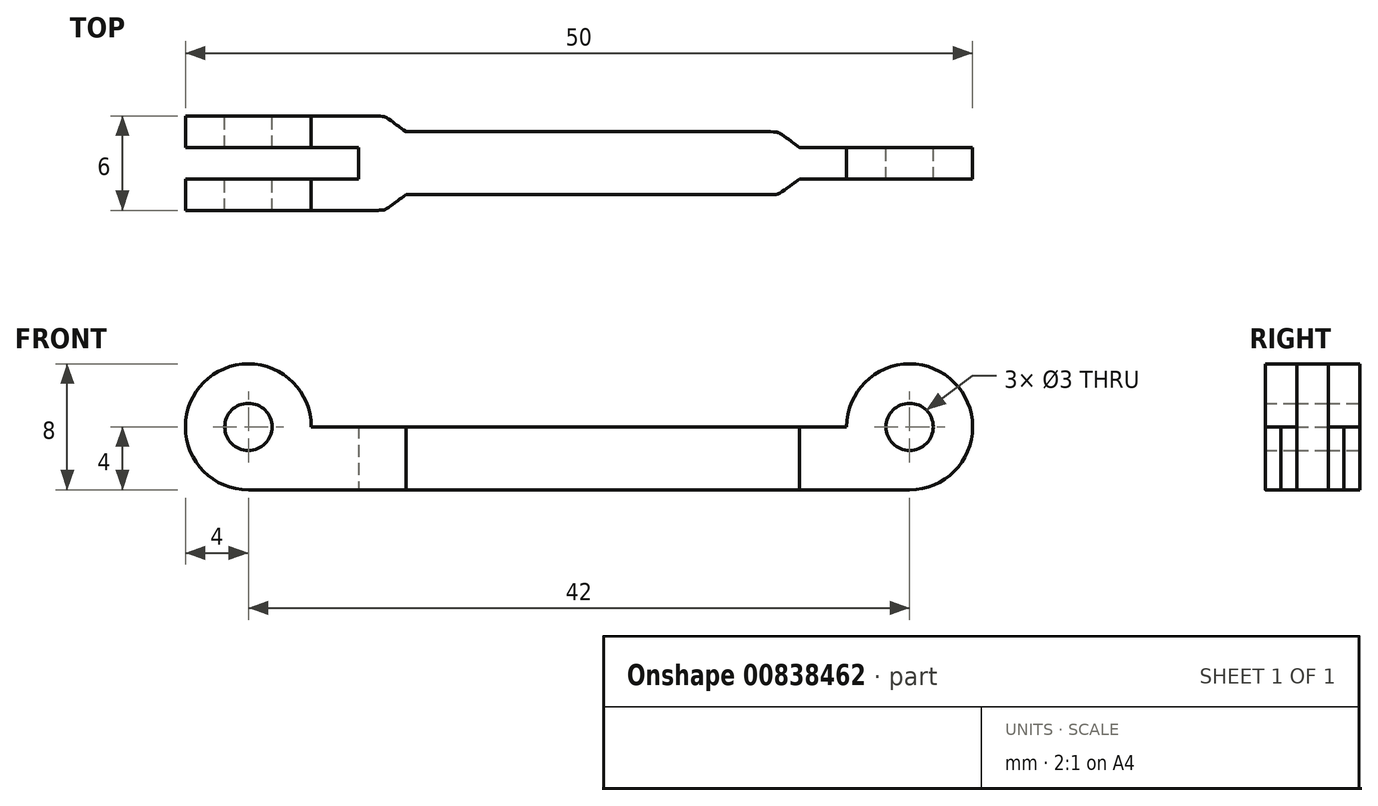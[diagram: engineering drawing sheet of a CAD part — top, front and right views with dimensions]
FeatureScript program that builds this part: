
annotation { "Feature Type Name" : "Feature", "Feature Type Description" : "" }
export const myFeature = defineFeature(function(context is Context, id is Id, definition is map)
    precondition{}
    {
        {
            var Q0;
            Q0=qCreatedBy(makeId("Front.planeOp"),FACE);
            var sketch = newSketch(context, id + "F0", { "sketchPlane" : qUnion([Q0])});
            skLineSegment(sketch, "E0.bottom", {"start": v(21, 2) * mm, "end": v(-21, 2) * mm});
            skLineSegment(sketch, "E0.top", {"start": v(21, -2) * mm, "end": v(-21, -2) * mm});
            skLineSegment(sketch, "E0.left", {"start": v(21, 2) * mm, "end": v(21, -2) * mm});
            skLineSegment(sketch, "E0.right", {"start": v(-21, 2) * mm, "end": v(-21, -2) * mm});
            skPoint(sketch, "E0.middle", {"position": v(0, 0) * mm});
            skLineSegment(sketch, "E1", {"start": v(-14, 2) * mm, "end": v(-14, -2) * mm});
            skLineSegment(sketch, "E2", {"start": v(-11, 2) * mm, "end": v(-11, -2) * mm});
            skCircle(sketch, "E3", {"center": v(21, 2) * mm, "radius": 4 * mm});
            skCircle(sketch, "E4", {"center": v(-21, 2) * mm, "radius": 4 * mm});
            skCircle(sketch, "E5", {"center": v(21, 2) * mm, "radius": 1.5 * mm});
            skCircle(sketch, "E6", {"center": v(-21, 2) * mm, "radius": 1.5 * mm});
            skLineSegment(sketch, "E7", {"start": v(14, 2) * mm, "end": v(14, -2) * mm});
            skSolve(sketch);
        }
        {
            var Q0;
            {var subQ0=sQuery(id+"F0.wireOp",EDGE,"E4");var subQ1=sQuery(id+"F0.wireOp",EDGE,"E0.bottom");var subQ2=makeQuery(id+"F0.imprint","INTERSECT",VERTEX,{"derivedFrom":[subQ1,subQ0]});Q0=makeQuery(id+"F0.imprint","IMPRINT",FACE,{"disambiguationData":[TD([[makeQuery(id+"F0.imprint","IMPRINT",EDGE,{"disambiguationData":[TD([[subQ2,-1.0]])],"derivedFrom":subQ1}),-1.0]])]});}
            var Q1;
            {var subQ0=sQuery(id+"F0.wireOp",EDGE,"E4");var subQ1=sQuery(id+"F0.wireOp",EDGE,"E0.bottom");var subQ2=makeQuery(id+"F0.imprint","INTERSECT",VERTEX,{"derivedFrom":[subQ1,subQ0]});Q1=makeQuery(id+"F0.imprint","IMPRINT",FACE,{"disambiguationData":[TD([[makeQuery(id+"F0.imprint","IMPRINT",EDGE,{"disambiguationData":[TD([[subQ2,-1.0]])],"derivedFrom":subQ1}),1.0]])]});}
            var Q2;
            {var subQ0=sQuery(id+"F0.wireOp",EDGE,"E1");Q2=makeQuery(id+"F0.imprint","IMPRINT",FACE,{"disambiguationData":[TD([[makeQuery(id+"F0.imprint","IMPRINT",EDGE,{"derivedFrom":subQ0}),-1.0]])]});}
            var Q3;
            {var subQ0=sQuery(id+"F0.wireOp",EDGE,"E1");Q3=makeQuery(id+"F0.imprint","IMPRINT",FACE,{"disambiguationData":[TD([[makeQuery(id+"F0.imprint","IMPRINT",EDGE,{"derivedFrom":subQ0}),1.0]])]});}
            extrude(context, id + "F1", {"entities" : qUnion([Q0, Q1, Q2, Q3]), "flatOperationType" : FlatOperationType.REMOVE, "depth" : 6 * mm, "offsetDistance" : 25 * mm, "domain" : OperationDomain.MODEL, "symmetric" : true});
        }
        {
            var Q0;
            {var subQ0=sQuery(id+"F0.wireOp",EDGE,"E2");Q0=makeQuery(id+"F0.imprint","IMPRINT",FACE,{"disambiguationData":[TD([[makeQuery(id+"F0.imprint","IMPRINT",EDGE,{"derivedFrom":subQ0}),1.0]])]});}
            extrude(context, id + "F2", {"entities" : qUnion([Q0]), "operationType" : NewBodyOperationType.ADD, "depth" : 4 * mm, "offsetDistance" : 25 * mm, "symmetric" : true});
        }
        {
            var Q0;
            {var subQ0=sQuery(id+"F0.wireOp",EDGE,"E7");Q0=makeQuery(id+"F0.imprint","IMPRINT",FACE,{"disambiguationData":[TD([[makeQuery(id+"F0.imprint","IMPRINT",EDGE,{"derivedFrom":subQ0}),1.0]])]});}
            var Q1;
            {var subQ0=sQuery(id+"F0.wireOp",EDGE,"E3");var subQ1=sQuery(id+"F0.wireOp",EDGE,"E0.bottom");var subQ2=makeQuery(id+"F0.imprint","INTERSECT",VERTEX,{"derivedFrom":[subQ1,subQ0]});Q1=makeQuery(id+"F0.imprint","IMPRINT",FACE,{"disambiguationData":[TD([[makeQuery(id+"F0.imprint","IMPRINT",EDGE,{"disambiguationData":[TD([[subQ2,1.0]])],"derivedFrom":subQ1}),1.0]])]});}
            var Q2;
            {var subQ0=sQuery(id+"F0.wireOp",EDGE,"E3");var subQ1=sQuery(id+"F0.wireOp",EDGE,"E0.bottom");var subQ2=makeQuery(id+"F0.imprint","INTERSECT",VERTEX,{"derivedFrom":[subQ1,subQ0]});Q2=makeQuery(id+"F0.imprint","IMPRINT",FACE,{"disambiguationData":[TD([[makeQuery(id+"F0.imprint","IMPRINT",EDGE,{"disambiguationData":[TD([[subQ2,1.0]])],"derivedFrom":subQ1}),-1.0]])]});}
            extrude(context, id + "F3", {"entities" : qUnion([Q0, Q1, Q2]), "operationType" : NewBodyOperationType.ADD, "depth" : 2 * mm, "offsetDistance" : 25 * mm, "symmetric" : true});
        }
        {
            var Q0;
            {var subQ0=sQuery(id+"F0.wireOp",EDGE,"E1");Q0=makeQuery(id+"F0.imprint","IMPRINT",FACE,{"disambiguationData":[TD([[makeQuery(id+"F0.imprint","IMPRINT",EDGE,{"derivedFrom":subQ0}),-1.0]])]});}
            var Q1;
            {var subQ0=sQuery(id+"F0.wireOp",EDGE,"E4");var subQ1=sQuery(id+"F0.wireOp",EDGE,"E0.bottom");var subQ2=makeQuery(id+"F0.imprint","INTERSECT",VERTEX,{"derivedFrom":[subQ1,subQ0]});Q1=makeQuery(id+"F0.imprint","IMPRINT",FACE,{"disambiguationData":[TD([[makeQuery(id+"F0.imprint","IMPRINT",EDGE,{"disambiguationData":[TD([[subQ2,-1.0]])],"derivedFrom":subQ1}),1.0]])]});}
            var Q2;
            {var subQ0=sQuery(id+"F0.wireOp",EDGE,"E4");var subQ1=sQuery(id+"F0.wireOp",EDGE,"E0.bottom");var subQ2=makeQuery(id+"F0.imprint","INTERSECT",VERTEX,{"derivedFrom":[subQ1,subQ0]});Q2=makeQuery(id+"F0.imprint","IMPRINT",FACE,{"disambiguationData":[TD([[makeQuery(id+"F0.imprint","IMPRINT",EDGE,{"disambiguationData":[TD([[subQ2,-1.0]])],"derivedFrom":subQ1}),-1.0]])]});}
            extrude(context, id + "F4", {"entities" : qUnion([Q0, Q1, Q2]), "operationType" : NewBodyOperationType.REMOVE, "flatOperationType" : FlatOperationType.REMOVE, "oppositeDirection" : true, "depth" : 2 * mm, "offsetDistance" : 25 * mm, "domain" : OperationDomain.MODEL, "symmetric" : true});
        }
        {
            var Q0;
            Q0=makeQuery(id+"F1.opExtrude","CAP_EDGE",EDGE,{"disambiguationData":[OSD([sQuery(id+"F0.wireOp",EDGE,"E2")])],"isStart":false});
            var Q1;
            Q1=makeQuery(id+"F2.opExtrude","CAP_EDGE",EDGE,{"disambiguationData":[OSD([sQuery(id+"F0.wireOp",EDGE,"E7")])],"isStart":false});
            var Q2;
            Q2=makeQuery(id+"F1.opExtrude","CAP_EDGE",EDGE,{"disambiguationData":[OSD([sQuery(id+"F0.wireOp",EDGE,"E2")])],"isStart":true});
            var Q3;
            Q3=makeQuery(id+"F2.opExtrude","CAP_EDGE",EDGE,{"disambiguationData":[OSD([sQuery(id+"F0.wireOp",EDGE,"E7")])],"isStart":true});
            fillet(context, id + "F5", {"entities" : qUnion([Q0, Q1, Q2, Q3]), "radius" : 5 * mm, "tangentPropagation" : true, "rho" : 0.9, "crossSection" : FilletCrossSection.CONIC, "allowEdgeOverflow" : false});
        }
    });
